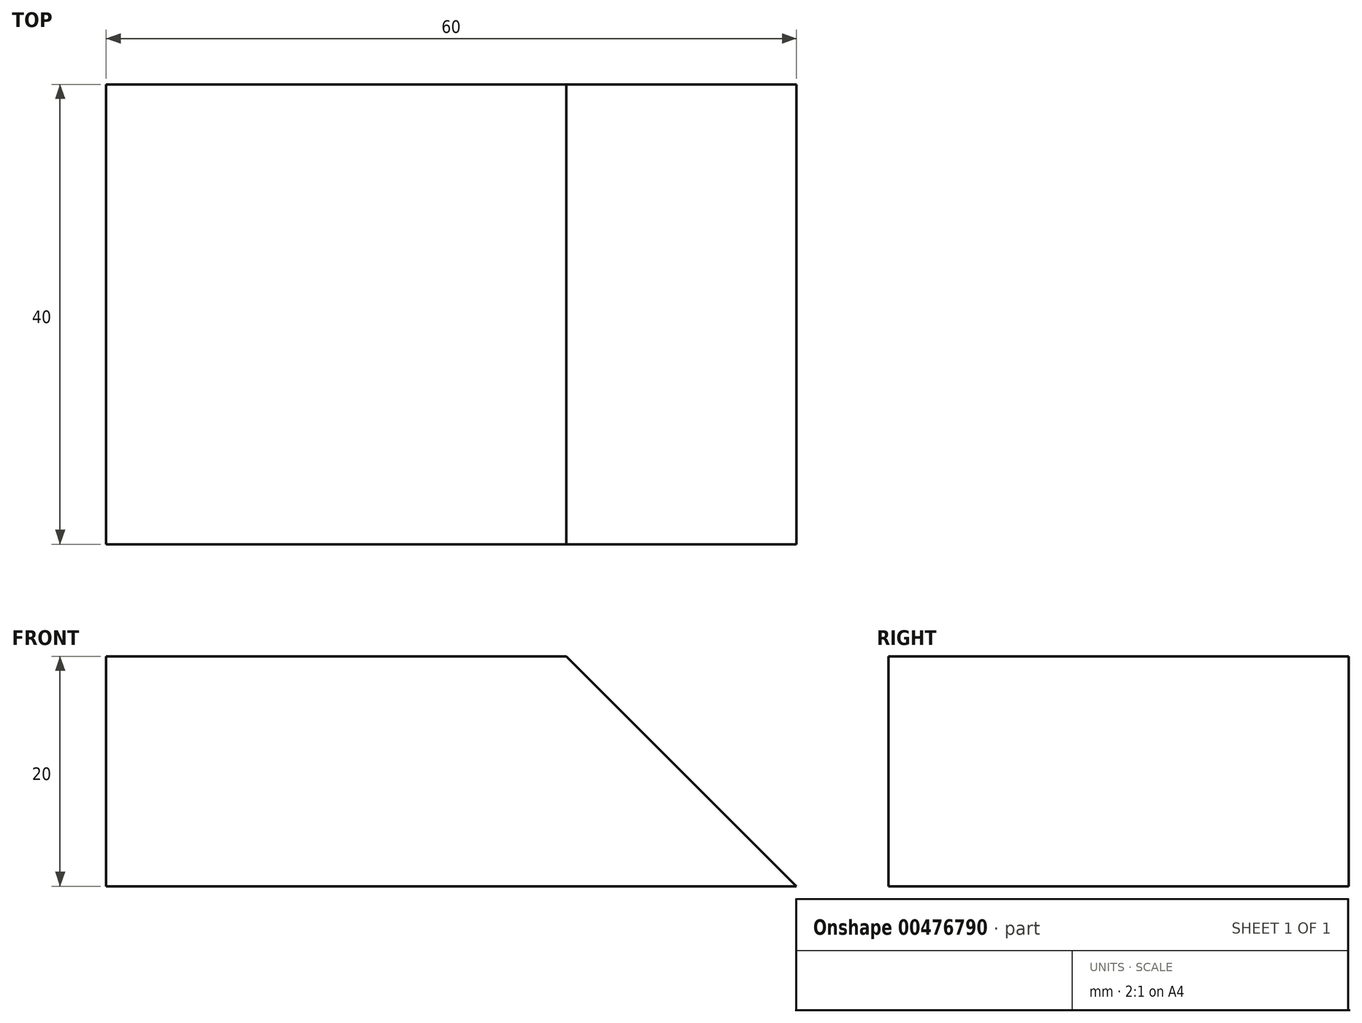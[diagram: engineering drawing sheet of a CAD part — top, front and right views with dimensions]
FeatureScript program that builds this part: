
annotation { "Feature Type Name" : "Feature", "Feature Type Description" : "" }
export const myFeature = defineFeature(function(context is Context, id is Id, definition is map)
    precondition{}
    {
        {
            var Q0;
            Q0=qCreatedBy(makeId("Front.planeOp"),FACE);
            var sketch = newSketch(context, id + "F0", { "sketchPlane" : qUnion([Q0])});
            skLineSegment(sketch, "E0", {"start": v(0, -10) * mm, "end": v(0, 0) * mm});
            skLineSegment(sketch, "E1", {"start": v(0, 0) * mm, "end": v(0, 10) * mm});
            skLineSegment(sketch, "E2", {"start": v(0, 10) * mm, "end": v(-30, 10) * mm});
            skLineSegment(sketch, "E3", {"start": v(-30, 10) * mm, "end": v(-30, -10) * mm});
            skLineSegment(sketch, "E4", {"start": v(-30, -10) * mm, "end": v(0, -10) * mm});
            skLineSegment(sketch, "E5", {"start": v(0, -10) * mm, "end": v(30, -10) * mm});
            skLineSegment(sketch, "E6", {"start": v(0, 10) * mm, "end": v(10, 10) * mm});
            skLineSegment(sketch, "E7", {"start": v(10, 10) * mm, "end": v(30, -10) * mm});
            skSolve(sketch);
        }
        {
            var Q0;
            Q0=makeQuery(id+"F0.imprint","IMPRINT",FACE,{"disambiguationData":[TD([[makeQuery(id+"F0.imprint","IMPRINT",EDGE,{"derivedFrom":sQuery(id+"F0.wireOp",EDGE,"E0")}),1.0]])]});
            var Q1;
            Q1=makeQuery(id+"F0.imprint","IMPRINT",FACE,{"disambiguationData":[TD([[makeQuery(id+"F0.imprint","IMPRINT",EDGE,{"derivedFrom":sQuery(id+"F0.wireOp",EDGE,"E0")}),-1.0]])]});
            extrude(context, id + "F1", {"entities" : qUnion([Q0, Q1]), "depth" : 40 * mm});
        }
    });
